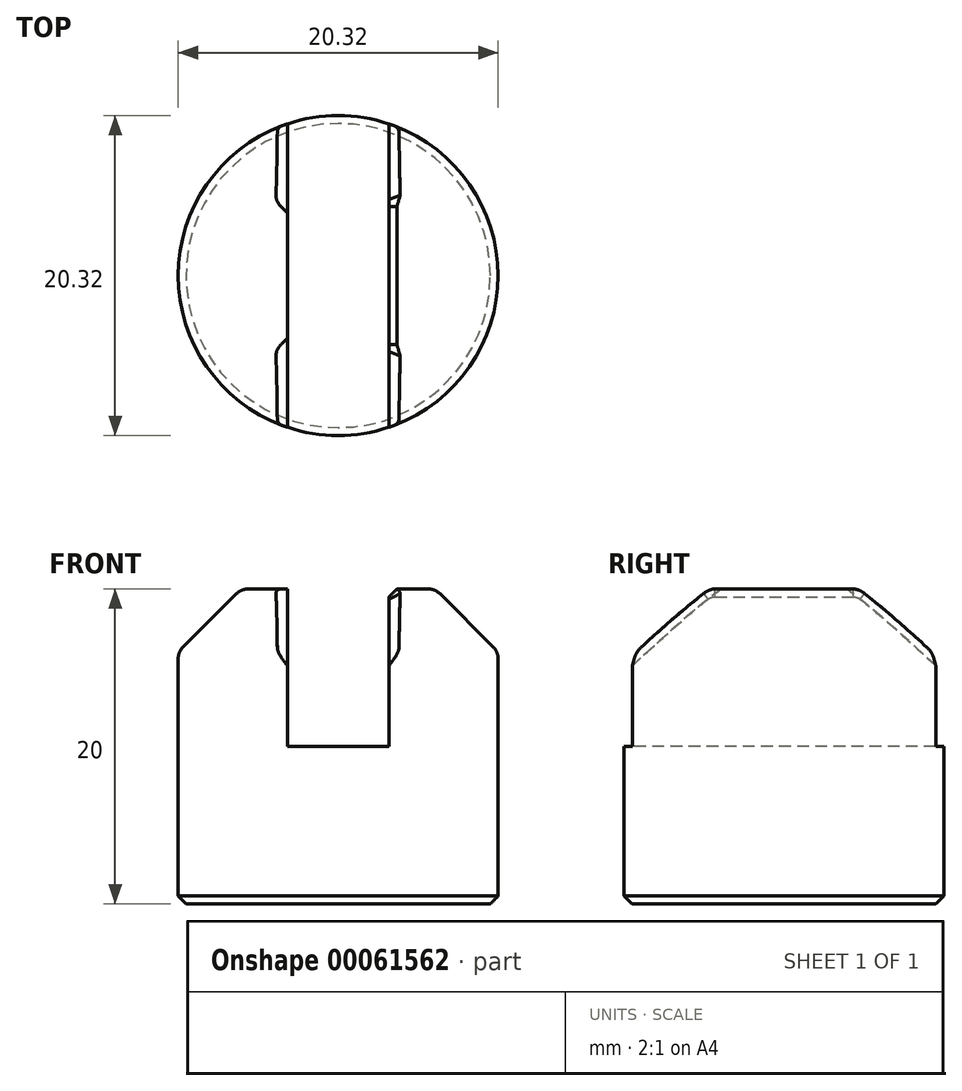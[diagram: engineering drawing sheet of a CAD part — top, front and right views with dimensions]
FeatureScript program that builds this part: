
annotation { "Feature Type Name" : "Feature", "Feature Type Description" : "" }
export const myFeature = defineFeature(function(context is Context, id is Id, definition is map)
    precondition{}
    {
        {
            var Q0;
            Q0=qCreatedBy(makeId("Top.planeOp"),FACE);
            var sketch = newSketch(context, id + "F0", { "sketchPlane" : qUnion([Q0])});
            skCircle(sketch, "E0", {"center": v(0, 0) * mm, "radius": 10.16 * mm});
            skSolve(sketch);
        }
        {
            var Q0;
            Q0=makeQuery(id+"F0.imprint","IMPRINT",FACE,{"disambiguationData":[TD([[makeQuery(id+"F0.imprint","IMPRINT",EDGE,{"derivedFrom":sQuery(id+"F0.wireOp",EDGE,"E0")}),1.0]])]});
            extrude(context, id + "F1", {"entities" : qUnion([Q0]), "depth" : 20 * mm});
        }
        {
            var Q0;
            Q0=makeQuery(id+"F1.opExtrude","CAP_FACE",FACE,{"disambiguationData":[OSD([sQuery(id+"F0.wireOp",EDGE,"E0")])],"isStart":false});
            var sketch = newSketch(context, id + "F2", { "sketchPlane" : qUnion([Q0])});
            skLineSegment(sketch, "E1.rect.bottom", {"start": v(-3.22, 19.15) * mm, "end": v(3.22, 19.15) * mm});
            skLineSegment(sketch, "E1.rect.top", {"start": v(-3.22, -19.15) * mm, "end": v(3.22, -19.15) * mm});
            skLineSegment(sketch, "E1.rect.left", {"start": v(-3.22, 19.15) * mm, "end": v(-3.22, -19.15) * mm});
            skLineSegment(sketch, "E1.rect.right", {"start": v(3.22, 19.15) * mm, "end": v(3.22, -19.15) * mm});
            skPoint(sketch, "E1.rect.middle", {"position": v(0, 0) * mm});
            skSolve(sketch);
        }
        {
            var Q0;
            {var subQ0=sQuery(id+"F2.wireOp",EDGE,"E1.rect.left");var subQ1=makeQuery(id+"F1.opExtrude","CAP_EDGE",EDGE,{"disambiguationData":[OSD([sQuery(id+"F0.wireOp",EDGE,"E0")])],"isStart":false});var subQ2=makeQuery(id+"F2.imprint","INTERSECT",VERTEX,{"disambiguationData":[OD(0.0)],"derivedFrom":[subQ1,subQ0]});Q0=makeQuery(id+"F2.imprint","IMPRINT",FACE,{"disambiguationData":[TD([[makeQuery(id+"F2.imprint","IMPRINT",EDGE,{"disambiguationData":[TD([[subQ2,-1.0]])],"derivedFrom":subQ0}),1.0]])]});}
            extrude(context, id + "F3", {"entities" : qUnion([Q0]), "operationType" : NewBodyOperationType.REMOVE, "oppositeDirection" : true, "depth" : 10 * mm});
        }
        {
            var Q0;
            {var subQ0=sQuery(id+"F0.wireOp",EDGE,"E0");Q0=makeQuery(id+"F3.boolean.opBoolean","SPLIT",EDGE,{"disambiguationData":[TD([makeQuery(id+"F3.opExtrude","SWEPT_FACE",FACE,{"disambiguationData":[OSD([sQuery(id+"F2.wireOp",EDGE,"E1.rect.left")])]})])],"derivedFrom":makeQuery(id+"F1.opExtrude","CAP_EDGE",EDGE,{"disambiguationData":[OSD([subQ0])],"isStart":false})});}
            var Q1;
            {var subQ0=sQuery(id+"F0.wireOp",EDGE,"E0");Q1=makeQuery(id+"F3.boolean.opBoolean","SPLIT",EDGE,{"disambiguationData":[TD([makeQuery(id+"F3.opExtrude","SWEPT_FACE",FACE,{"disambiguationData":[OSD([sQuery(id+"F2.wireOp",EDGE,"E1.rect.right")])]})])],"derivedFrom":makeQuery(id+"F1.opExtrude","CAP_EDGE",EDGE,{"disambiguationData":[OSD([subQ0])],"isStart":false})});}
            chamfer(context, id + "F4", {"entities" : qUnion([Q0, Q1]), "width" : 4 * mm, "tangentPropagation" : true});
        }
        {
            var Q0;
            {var subQ0=sQuery(id+"F0.wireOp",EDGE,"E0");var subQ1=makeQuery(id+"F1.opExtrude","SWEPT_FACE",FACE,{"disambiguationData":[OSD([subQ0])]});Q0=makeQuery(id+"F4.opChamfer","BLEND_EDGE",EDGE,{"blendedFrom":[makeQuery(id+"F3.boolean.opBoolean","SPLIT",EDGE,{"disambiguationData":[TD([makeQuery(id+"F3.opExtrude","SWEPT_FACE",FACE,{"disambiguationData":[OSD([sQuery(id+"F2.wireOp",EDGE,"E1.rect.left")])]})])],"derivedFrom":makeQuery(id+"F1.opExtrude","CAP_EDGE",EDGE,{"disambiguationData":[OSD([subQ0])],"isStart":false})}),subQ1],"blendedInto":[subQ1]});}
            var Q1;
            {var subQ0=sQuery(id+"F0.wireOp",EDGE,"E0");var subQ2=makeQuery(id+"F3.opExtrude","SWEPT_FACE",FACE,{"disambiguationData":[OSD([sQuery(id+"F2.wireOp",EDGE,"E1.rect.left")])]});var subQ3=makeQuery(id+"F1.opExtrude","CAP_FACE",FACE,{"disambiguationData":[OSD([subQ0])],"isStart":false});Q1=makeQuery(id+"F4.opChamfer","BLEND_EDGE",EDGE,{"blendedFrom":[makeQuery(id+"F3.boolean.opBoolean","SPLIT",EDGE,{"disambiguationData":[TD([subQ2])],"derivedFrom":makeQuery(id+"F1.opExtrude","CAP_EDGE",EDGE,{"disambiguationData":[OSD([subQ0])],"isStart":false})}),makeQuery(id+"F3.boolean.opBoolean","SPLIT",FACE,{"disambiguationData":[TD([subQ2])],"derivedFrom":subQ3})],"blendedInto":[makeQuery(id+"F3.boolean.opBoolean","SPLIT",FACE,{"disambiguationData":[TD([subQ2])],"derivedFrom":subQ3})]});}
            var Q2;
            {var subQ0=sQuery(id+"F0.wireOp",EDGE,"E0");var subQ1=makeQuery(id+"F1.opExtrude","SWEPT_FACE",FACE,{"disambiguationData":[OSD([subQ0])]});Q2=makeQuery(id+"F4.opChamfer","BLEND_EDGE",EDGE,{"blendedFrom":[makeQuery(id+"F3.boolean.opBoolean","SPLIT",EDGE,{"disambiguationData":[TD([makeQuery(id+"F3.opExtrude","SWEPT_FACE",FACE,{"disambiguationData":[OSD([sQuery(id+"F2.wireOp",EDGE,"E1.rect.right")])]})])],"derivedFrom":makeQuery(id+"F1.opExtrude","CAP_EDGE",EDGE,{"disambiguationData":[OSD([subQ0])],"isStart":false})}),subQ1],"blendedInto":[subQ1]});}
            var Q3;
            {var subQ0=sQuery(id+"F0.wireOp",EDGE,"E0");var subQ2=makeQuery(id+"F3.opExtrude","SWEPT_FACE",FACE,{"disambiguationData":[OSD([sQuery(id+"F2.wireOp",EDGE,"E1.rect.right")])]});var subQ3=makeQuery(id+"F1.opExtrude","CAP_FACE",FACE,{"disambiguationData":[OSD([subQ0])],"isStart":false});Q3=makeQuery(id+"F4.opChamfer","BLEND_EDGE",EDGE,{"blendedFrom":[makeQuery(id+"F3.boolean.opBoolean","SPLIT",EDGE,{"disambiguationData":[TD([subQ2])],"derivedFrom":makeQuery(id+"F1.opExtrude","CAP_EDGE",EDGE,{"disambiguationData":[OSD([subQ0])],"isStart":false})}),makeQuery(id+"F3.boolean.opBoolean","SPLIT",FACE,{"disambiguationData":[TD([subQ2])],"derivedFrom":subQ3})],"blendedInto":[makeQuery(id+"F3.boolean.opBoolean","SPLIT",FACE,{"disambiguationData":[TD([subQ2])],"derivedFrom":subQ3})]});}
            fillet(context, id + "F5", {"entities" : qUnion([Q0, Q1, Q2, Q3]), "radius" : 1 * mm, "tangentPropagation" : true, "allowEdgeOverflow" : false});
        }
        {
            var Q0;
            Q0=makeQuery(id+"F1.opExtrude","CAP_FACE",FACE,{"disambiguationData":[OSD([sQuery(id+"F0.wireOp",EDGE,"E0")])],"isStart":true});
            chamfer(context, id + "F6", {"entities" : qUnion([Q0]), "width" : .5 * mm, "tangentPropagation" : true});
        }
        {
            var Q0;
            {var subQ0=makeQuery(id+"F3.opExtrude","SWEPT_FACE",FACE,{"disambiguationData":[OSD([sQuery(id+"F2.wireOp",EDGE,"E1.rect.left")])]});var subQ1=sQuery(id+"F0.wireOp",EDGE,"E0");Q0=makeQuery(id+"F4.opChamfer","BLEND_EDGE",EDGE,{"disambiguationData":[OD(0.0)],"blendedFrom":[makeQuery(id+"F3.boolean.opBoolean","SPLIT",EDGE,{"disambiguationData":[TD([subQ0])],"derivedFrom":makeQuery(id+"F1.opExtrude","CAP_EDGE",EDGE,{"disambiguationData":[OSD([subQ1])],"isStart":false})}),makeQuery(id+"F3.boolean.opBoolean","COPY",FACE,{"derivedFrom":subQ0})],"blendedInto":[makeQuery(id+"F3.boolean.opBoolean","COPY",FACE,{"derivedFrom":subQ0})]});}
            var Q1;
            {var subQ0=makeQuery(id+"F3.opExtrude","SWEPT_FACE",FACE,{"disambiguationData":[OSD([sQuery(id+"F2.wireOp",EDGE,"E1.rect.left")])]});var subQ1=sQuery(id+"F0.wireOp",EDGE,"E0");var subQ3=makeQuery(id+"F1.opExtrude","CAP_FACE",FACE,{"disambiguationData":[OSD([subQ1])],"isStart":false});Q1=makeQuery(id+"F5.opFillet","BLEND_EDGE",EDGE,{"disambiguationData":[OD(0.0)],"blendedFrom":[makeQuery(id+"F4.opChamfer","BLEND_EDGE",EDGE,{"blendedFrom":[makeQuery(id+"F3.boolean.opBoolean","SPLIT",EDGE,{"disambiguationData":[TD([subQ0])],"derivedFrom":makeQuery(id+"F1.opExtrude","CAP_EDGE",EDGE,{"disambiguationData":[OSD([subQ1])],"isStart":false})}),makeQuery(id+"F3.boolean.opBoolean","SPLIT",FACE,{"disambiguationData":[TD([subQ0])],"derivedFrom":subQ3})],"blendedInto":[makeQuery(id+"F3.boolean.opBoolean","SPLIT",FACE,{"disambiguationData":[TD([subQ0])],"derivedFrom":subQ3})]}),makeQuery(id+"F3.boolean.opBoolean","COPY",FACE,{"derivedFrom":subQ0})],"blendedInto":[makeQuery(id+"F3.boolean.opBoolean","COPY",FACE,{"derivedFrom":subQ0})]});}
            var Q2;
            {var subQ0=makeQuery(id+"F3.opExtrude","SWEPT_FACE",FACE,{"disambiguationData":[OSD([sQuery(id+"F2.wireOp",EDGE,"E1.rect.left")])]});var subQ1=sQuery(id+"F0.wireOp",EDGE,"E0");var subQ2=makeQuery(id+"F1.opExtrude","SWEPT_FACE",FACE,{"disambiguationData":[OSD([subQ1])]});Q2=makeQuery(id+"F5.opFillet","BLEND_EDGE",EDGE,{"disambiguationData":[OD(0.0)],"blendedFrom":[makeQuery(id+"F4.opChamfer","BLEND_EDGE",EDGE,{"blendedFrom":[makeQuery(id+"F3.boolean.opBoolean","SPLIT",EDGE,{"disambiguationData":[TD([subQ0])],"derivedFrom":makeQuery(id+"F1.opExtrude","CAP_EDGE",EDGE,{"disambiguationData":[OSD([subQ1])],"isStart":false})}),subQ2],"blendedInto":[subQ2]}),makeQuery(id+"F3.boolean.opBoolean","COPY",FACE,{"derivedFrom":subQ0})],"blendedInto":[makeQuery(id+"F3.boolean.opBoolean","COPY",FACE,{"derivedFrom":subQ0})]});}
            var Q3;
            {var subQ0=sQuery(id+"F2.wireOp",EDGE,"E1.rect.left");var subQ1=sQuery(id+"F0.wireOp",EDGE,"E0");Q3=makeQuery(id+"F3.boolean.opBoolean","COPY",EDGE,{"derivedFrom":makeQuery(id+"F3.opExtrude","SWEPT_EDGE",EDGE,{"disambiguationData":[OSD([subQ1,subQ0]),TDD([makeQuery(id+"F2.imprint","INTERSECT",VERTEX,{"disambiguationData":[OD(0.0)],"derivedFrom":[makeQuery(id+"F1.opExtrude","CAP_EDGE",EDGE,{"disambiguationData":[OSD([subQ1])],"isStart":false}),subQ0]})])]})});}
            var Q4;
            Q4=makeQuery(id+"F3.boolean.opBoolean","COPY",EDGE,{"derivedFrom":makeQuery(id+"F3.opExtrude","CAP_EDGE",EDGE,{"disambiguationData":[OSD([sQuery(id+"F2.wireOp",EDGE,"E1.rect.left")])],"isStart":true})});
            var Q5;
            {var subQ0=makeQuery(id+"F3.opExtrude","SWEPT_FACE",FACE,{"disambiguationData":[OSD([sQuery(id+"F2.wireOp",EDGE,"E1.rect.left")])]});var subQ1=sQuery(id+"F0.wireOp",EDGE,"E0");var subQ3=makeQuery(id+"F1.opExtrude","CAP_FACE",FACE,{"disambiguationData":[OSD([subQ1])],"isStart":false});Q5=makeQuery(id+"F5.opFillet","BLEND_EDGE",EDGE,{"disambiguationData":[OD(1.0)],"blendedFrom":[makeQuery(id+"F4.opChamfer","BLEND_EDGE",EDGE,{"blendedFrom":[makeQuery(id+"F3.boolean.opBoolean","SPLIT",EDGE,{"disambiguationData":[TD([subQ0])],"derivedFrom":makeQuery(id+"F1.opExtrude","CAP_EDGE",EDGE,{"disambiguationData":[OSD([subQ1])],"isStart":false})}),makeQuery(id+"F3.boolean.opBoolean","SPLIT",FACE,{"disambiguationData":[TD([subQ0])],"derivedFrom":subQ3})],"blendedInto":[makeQuery(id+"F3.boolean.opBoolean","SPLIT",FACE,{"disambiguationData":[TD([subQ0])],"derivedFrom":subQ3})]}),makeQuery(id+"F3.boolean.opBoolean","COPY",FACE,{"derivedFrom":subQ0})],"blendedInto":[makeQuery(id+"F3.boolean.opBoolean","COPY",FACE,{"derivedFrom":subQ0})]});}
            var Q6;
            {var subQ0=makeQuery(id+"F3.opExtrude","SWEPT_FACE",FACE,{"disambiguationData":[OSD([sQuery(id+"F2.wireOp",EDGE,"E1.rect.left")])]});var subQ1=sQuery(id+"F0.wireOp",EDGE,"E0");Q6=makeQuery(id+"F4.opChamfer","BLEND_EDGE",EDGE,{"disambiguationData":[OD(1.0)],"blendedFrom":[makeQuery(id+"F3.boolean.opBoolean","SPLIT",EDGE,{"disambiguationData":[TD([subQ0])],"derivedFrom":makeQuery(id+"F1.opExtrude","CAP_EDGE",EDGE,{"disambiguationData":[OSD([subQ1])],"isStart":false})}),makeQuery(id+"F3.boolean.opBoolean","COPY",FACE,{"derivedFrom":subQ0})],"blendedInto":[makeQuery(id+"F3.boolean.opBoolean","COPY",FACE,{"derivedFrom":subQ0})]});}
            var Q7;
            {var subQ0=makeQuery(id+"F3.opExtrude","SWEPT_FACE",FACE,{"disambiguationData":[OSD([sQuery(id+"F2.wireOp",EDGE,"E1.rect.left")])]});var subQ1=sQuery(id+"F0.wireOp",EDGE,"E0");var subQ2=makeQuery(id+"F1.opExtrude","SWEPT_FACE",FACE,{"disambiguationData":[OSD([subQ1])]});Q7=makeQuery(id+"F5.opFillet","BLEND_EDGE",EDGE,{"disambiguationData":[OD(1.0)],"blendedFrom":[makeQuery(id+"F4.opChamfer","BLEND_EDGE",EDGE,{"blendedFrom":[makeQuery(id+"F3.boolean.opBoolean","SPLIT",EDGE,{"disambiguationData":[TD([subQ0])],"derivedFrom":makeQuery(id+"F1.opExtrude","CAP_EDGE",EDGE,{"disambiguationData":[OSD([subQ1])],"isStart":false})}),subQ2],"blendedInto":[subQ2]}),makeQuery(id+"F3.boolean.opBoolean","COPY",FACE,{"derivedFrom":subQ0})],"blendedInto":[makeQuery(id+"F3.boolean.opBoolean","COPY",FACE,{"derivedFrom":subQ0})]});}
            var Q8;
            {var subQ0=sQuery(id+"F2.wireOp",EDGE,"E1.rect.left");var subQ1=sQuery(id+"F0.wireOp",EDGE,"E0");Q8=makeQuery(id+"F3.boolean.opBoolean","COPY",EDGE,{"derivedFrom":makeQuery(id+"F3.opExtrude","SWEPT_EDGE",EDGE,{"disambiguationData":[OSD([subQ1,subQ0]),TDD([makeQuery(id+"F2.imprint","INTERSECT",VERTEX,{"disambiguationData":[OD(1.0)],"derivedFrom":[makeQuery(id+"F1.opExtrude","CAP_EDGE",EDGE,{"disambiguationData":[OSD([subQ1])],"isStart":false}),subQ0]})])]})});}
            var Q9;
            {var subQ0=sQuery(id+"F2.wireOp",EDGE,"E1.rect.right");var subQ1=sQuery(id+"F0.wireOp",EDGE,"E0");Q9=makeQuery(id+"F3.boolean.opBoolean","COPY",EDGE,{"derivedFrom":makeQuery(id+"F3.opExtrude","SWEPT_EDGE",EDGE,{"disambiguationData":[OSD([subQ1,subQ0]),TDD([makeQuery(id+"F2.imprint","INTERSECT",VERTEX,{"disambiguationData":[OD(0.0)],"derivedFrom":[makeQuery(id+"F1.opExtrude","CAP_EDGE",EDGE,{"disambiguationData":[OSD([subQ1])],"isStart":false}),subQ0]})])]})});}
            var Q10;
            {var subQ0=sQuery(id+"F2.wireOp",EDGE,"E1.rect.right");var subQ1=sQuery(id+"F0.wireOp",EDGE,"E0");Q10=makeQuery(id+"F3.boolean.opBoolean","COPY",EDGE,{"derivedFrom":makeQuery(id+"F3.opExtrude","SWEPT_EDGE",EDGE,{"disambiguationData":[OSD([subQ1,subQ0]),TDD([makeQuery(id+"F2.imprint","INTERSECT",VERTEX,{"disambiguationData":[OD(1.0)],"derivedFrom":[makeQuery(id+"F1.opExtrude","CAP_EDGE",EDGE,{"disambiguationData":[OSD([subQ1])],"isStart":false}),subQ0]})])]})});}
            var Q11;
            {var subQ0=makeQuery(id+"F3.opExtrude","SWEPT_FACE",FACE,{"disambiguationData":[OSD([sQuery(id+"F2.wireOp",EDGE,"E1.rect.right")])]});var subQ1=sQuery(id+"F0.wireOp",EDGE,"E0");var subQ2=makeQuery(id+"F1.opExtrude","SWEPT_FACE",FACE,{"disambiguationData":[OSD([subQ1])]});Q11=makeQuery(id+"F5.opFillet","BLEND_EDGE",EDGE,{"disambiguationData":[OD(0.0)],"blendedFrom":[makeQuery(id+"F4.opChamfer","BLEND_EDGE",EDGE,{"blendedFrom":[makeQuery(id+"F3.boolean.opBoolean","SPLIT",EDGE,{"disambiguationData":[TD([subQ0])],"derivedFrom":makeQuery(id+"F1.opExtrude","CAP_EDGE",EDGE,{"disambiguationData":[OSD([subQ1])],"isStart":false})}),subQ2],"blendedInto":[subQ2]}),makeQuery(id+"F3.boolean.opBoolean","COPY",FACE,{"derivedFrom":subQ0})],"blendedInto":[makeQuery(id+"F3.boolean.opBoolean","COPY",FACE,{"derivedFrom":subQ0})]});}
            var Q12;
            {var subQ0=makeQuery(id+"F3.opExtrude","SWEPT_FACE",FACE,{"disambiguationData":[OSD([sQuery(id+"F2.wireOp",EDGE,"E1.rect.right")])]});var subQ1=sQuery(id+"F0.wireOp",EDGE,"E0");Q12=makeQuery(id+"F4.opChamfer","BLEND_EDGE",EDGE,{"disambiguationData":[OD(0.0)],"blendedFrom":[makeQuery(id+"F3.boolean.opBoolean","SPLIT",EDGE,{"disambiguationData":[TD([subQ0])],"derivedFrom":makeQuery(id+"F1.opExtrude","CAP_EDGE",EDGE,{"disambiguationData":[OSD([subQ1])],"isStart":false})}),makeQuery(id+"F3.boolean.opBoolean","COPY",FACE,{"derivedFrom":subQ0})],"blendedInto":[makeQuery(id+"F3.boolean.opBoolean","COPY",FACE,{"derivedFrom":subQ0})]});}
            var Q13;
            {var subQ0=makeQuery(id+"F3.opExtrude","SWEPT_FACE",FACE,{"disambiguationData":[OSD([sQuery(id+"F2.wireOp",EDGE,"E1.rect.right")])]});var subQ1=sQuery(id+"F0.wireOp",EDGE,"E0");var subQ3=makeQuery(id+"F1.opExtrude","CAP_FACE",FACE,{"disambiguationData":[OSD([subQ1])],"isStart":false});Q13=makeQuery(id+"F5.opFillet","BLEND_EDGE",EDGE,{"disambiguationData":[OD(0.0)],"blendedFrom":[makeQuery(id+"F4.opChamfer","BLEND_EDGE",EDGE,{"blendedFrom":[makeQuery(id+"F3.boolean.opBoolean","SPLIT",EDGE,{"disambiguationData":[TD([subQ0])],"derivedFrom":makeQuery(id+"F1.opExtrude","CAP_EDGE",EDGE,{"disambiguationData":[OSD([subQ1])],"isStart":false})}),makeQuery(id+"F3.boolean.opBoolean","SPLIT",FACE,{"disambiguationData":[TD([subQ0])],"derivedFrom":subQ3})],"blendedInto":[makeQuery(id+"F3.boolean.opBoolean","SPLIT",FACE,{"disambiguationData":[TD([subQ0])],"derivedFrom":subQ3})]}),makeQuery(id+"F3.boolean.opBoolean","COPY",FACE,{"derivedFrom":subQ0})],"blendedInto":[makeQuery(id+"F3.boolean.opBoolean","COPY",FACE,{"derivedFrom":subQ0})]});}
            var Q14;
            Q14=makeQuery(id+"F3.boolean.opBoolean","COPY",EDGE,{"derivedFrom":makeQuery(id+"F3.opExtrude","CAP_EDGE",EDGE,{"disambiguationData":[OSD([sQuery(id+"F2.wireOp",EDGE,"E1.rect.right")])],"isStart":true})});
            var Q15;
            {var subQ0=makeQuery(id+"F3.opExtrude","SWEPT_FACE",FACE,{"disambiguationData":[OSD([sQuery(id+"F2.wireOp",EDGE,"E1.rect.right")])]});var subQ1=sQuery(id+"F0.wireOp",EDGE,"E0");var subQ3=makeQuery(id+"F1.opExtrude","CAP_FACE",FACE,{"disambiguationData":[OSD([subQ1])],"isStart":false});Q15=makeQuery(id+"F5.opFillet","BLEND_EDGE",EDGE,{"disambiguationData":[OD(1.0)],"blendedFrom":[makeQuery(id+"F4.opChamfer","BLEND_EDGE",EDGE,{"blendedFrom":[makeQuery(id+"F3.boolean.opBoolean","SPLIT",EDGE,{"disambiguationData":[TD([subQ0])],"derivedFrom":makeQuery(id+"F1.opExtrude","CAP_EDGE",EDGE,{"disambiguationData":[OSD([subQ1])],"isStart":false})}),makeQuery(id+"F3.boolean.opBoolean","SPLIT",FACE,{"disambiguationData":[TD([subQ0])],"derivedFrom":subQ3})],"blendedInto":[makeQuery(id+"F3.boolean.opBoolean","SPLIT",FACE,{"disambiguationData":[TD([subQ0])],"derivedFrom":subQ3})]}),makeQuery(id+"F3.boolean.opBoolean","COPY",FACE,{"derivedFrom":subQ0})],"blendedInto":[makeQuery(id+"F3.boolean.opBoolean","COPY",FACE,{"derivedFrom":subQ0})]});}
            var Q16;
            {var subQ0=makeQuery(id+"F3.opExtrude","SWEPT_FACE",FACE,{"disambiguationData":[OSD([sQuery(id+"F2.wireOp",EDGE,"E1.rect.right")])]});var subQ1=sQuery(id+"F0.wireOp",EDGE,"E0");Q16=makeQuery(id+"F4.opChamfer","BLEND_EDGE",EDGE,{"disambiguationData":[OD(1.0)],"blendedFrom":[makeQuery(id+"F3.boolean.opBoolean","SPLIT",EDGE,{"disambiguationData":[TD([subQ0])],"derivedFrom":makeQuery(id+"F1.opExtrude","CAP_EDGE",EDGE,{"disambiguationData":[OSD([subQ1])],"isStart":false})}),makeQuery(id+"F3.boolean.opBoolean","COPY",FACE,{"derivedFrom":subQ0})],"blendedInto":[makeQuery(id+"F3.boolean.opBoolean","COPY",FACE,{"derivedFrom":subQ0})]});}
            var Q17;
            {var subQ0=makeQuery(id+"F3.opExtrude","SWEPT_FACE",FACE,{"disambiguationData":[OSD([sQuery(id+"F2.wireOp",EDGE,"E1.rect.right")])]});var subQ1=sQuery(id+"F0.wireOp",EDGE,"E0");var subQ2=makeQuery(id+"F1.opExtrude","SWEPT_FACE",FACE,{"disambiguationData":[OSD([subQ1])]});Q17=makeQuery(id+"F5.opFillet","BLEND_EDGE",EDGE,{"disambiguationData":[OD(1.0)],"blendedFrom":[makeQuery(id+"F4.opChamfer","BLEND_EDGE",EDGE,{"blendedFrom":[makeQuery(id+"F3.boolean.opBoolean","SPLIT",EDGE,{"disambiguationData":[TD([subQ0])],"derivedFrom":makeQuery(id+"F1.opExtrude","CAP_EDGE",EDGE,{"disambiguationData":[OSD([subQ1])],"isStart":false})}),subQ2],"blendedInto":[subQ2]}),makeQuery(id+"F3.boolean.opBoolean","COPY",FACE,{"derivedFrom":subQ0})],"blendedInto":[makeQuery(id+"F3.boolean.opBoolean","COPY",FACE,{"derivedFrom":subQ0})]});}
            chamfer(context, id + "F7", {"entities" : qUnion([Q0, Q1, Q2, Q3, Q4, Q5, Q6, Q7, Q8, Q9, Q10, Q11, Q12, Q13, Q14, Q15, Q16, Q17]), "width" : .5 * mm});
        }
    });
